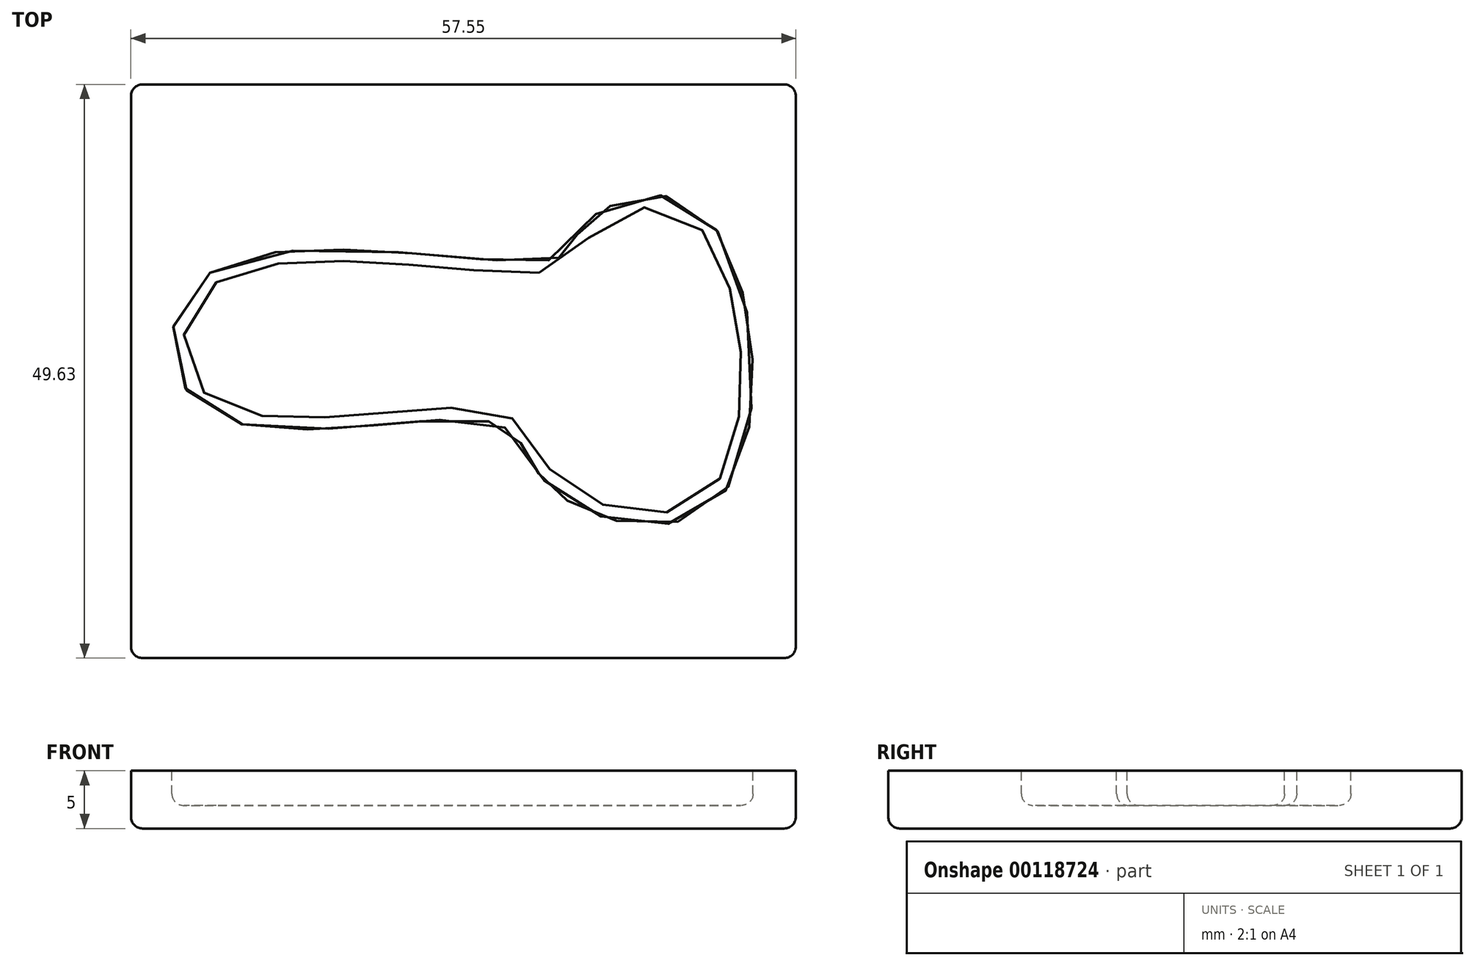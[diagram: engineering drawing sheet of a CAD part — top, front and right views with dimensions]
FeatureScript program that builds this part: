
annotation { "Feature Type Name" : "Feature", "Feature Type Description" : "" }
export const myFeature = defineFeature(function(context is Context, id is Id, definition is map)
    precondition{}
    {
        {
            var Q0;
            Q0=qCreatedBy(makeId("Top.planeOp"),FACE);
            var sketch = newSketch(context, id + "F0", { "sketchPlane" : qUnion([Q0])});
            skLineSegment(sketch, "E0.bottom", {"start": v(-57.55, 0) * mm, "end": v(0, 0) * mm});
            skLineSegment(sketch, "E0.top", {"start": v(-57.55, 49.63) * mm, "end": v(0, 49.63) * mm});
            skLineSegment(sketch, "E0.left", {"start": v(-57.55, 0) * mm, "end": v(-57.55, 49.63) * mm});
            skLineSegment(sketch, "E0.right", {"start": v(0, 0) * mm, "end": v(0, 49.63) * mm});
            skSolve(sketch);
        }
        {
            var Q0;
            Q0=makeQuery(id+"F0.imprint","IMPRINT",FACE,{"disambiguationData":[TD([[makeQuery(id+"F0.imprint","IMPRINT",EDGE,{"derivedFrom":sQuery(id+"F0.wireOp",EDGE,"E0.bottom")}),1.0]])]});
            extrude(context, id + "F1", {"entities" : qUnion([Q0]), "depth" : 5 * mm});
        }
        {
            var Q0;
            Q0=makeQuery(id+"F1.opExtrude","CAP_FACE",FACE,{"disambiguationData":[OSD([sQuery(id+"F0.wireOp",EDGE,"E0.bottom"),sQuery(id+"F0.wireOp",EDGE,"E0.top"),sQuery(id+"F0.wireOp",EDGE,"E0.left"),sQuery(id+"F0.wireOp",EDGE,"E0.right")])],"isStart":false});
            var sketch = newSketch(context, id + "F2", { "sketchPlane" : qUnion([Q0])});
            skFitSpline(sketch, "E1", {"points": [v(-50.7, 33.35) * mm, v(-20.78, 34.55) * mm, v(-18.4, 37.42) * mm, v(-8.54, 38.87) * mm, v(-6.24, 14.26) * mm, v(-18.4, 12.87) * mm, v(-22.88, 16.97) * mm, v(-26.54, 20.46) * mm, v(-50.99, 21.47) * mm, v(-50.7, 33.35) * mm]});
            skSolve(sketch);
        }
        {
            var Q0;
            Q0=makeQuery(id+"F2.imprint","IMPRINT",FACE,{"disambiguationData":[TD([[makeQuery(id+"F2.imprint","IMPRINT",EDGE,{"derivedFrom":sQuery(id+"F2.wireOp",EDGE,"E1")}),-1.0]])]});
            extrude(context, id + "F3", {"entities" : qUnion([Q0]), "operationType" : NewBodyOperationType.REMOVE, "oppositeDirection" : true, "depth" : 3 * mm});
        }
        {
            var Q0;
            Q0=makeQuery(id+"F3.boolean.opBoolean","COPY",FACE,{"derivedFrom":makeQuery(id+"F3.opExtrude","CAP_FACE",FACE,{"disambiguationData":[OSD([sQuery(id+"F2.wireOp",EDGE,"E1")])],"isStart":false})});
            fillet(context, id + "F4", {"entities" : qUnion([Q0]), "radius" : 1 * mm, "tangentPropagation" : true, "allowEdgeOverflow" : false});
        }
        {
            var Q0;
            Q0=makeQuery(id+"F1.opExtrude","CAP_FACE",FACE,{"disambiguationData":[OSD([sQuery(id+"F0.wireOp",EDGE,"E0.bottom"),sQuery(id+"F0.wireOp",EDGE,"E0.top"),sQuery(id+"F0.wireOp",EDGE,"E0.left"),sQuery(id+"F0.wireOp",EDGE,"E0.right")])],"isStart":true});
            fillet(context, id + "F5", {"entities" : qUnion([Q0]), "radius" : 1 * mm, "tangentPropagation" : true, "allowEdgeOverflow" : false});
        }
        {
            var Q0;
            Q0=makeQuery(id+"F1.opExtrude","SWEPT_EDGE",EDGE,{"disambiguationData":[OSD([sQuery(id+"F0.wireOp",EDGE,"E0.top"),sQuery(id+"F0.wireOp",EDGE,"E0.left")])]});
            var Q1;
            Q1=makeQuery(id+"F1.opExtrude","SWEPT_EDGE",EDGE,{"disambiguationData":[OSD([sQuery(id+"F0.wireOp",EDGE,"E0.bottom"),sQuery(id+"F0.wireOp",EDGE,"E0.right")])]});
            var Q2;
            Q2=makeQuery(id+"F1.opExtrude","SWEPT_EDGE",EDGE,{"disambiguationData":[OSD([sQuery(id+"F0.wireOp",EDGE,"E0.top"),sQuery(id+"F0.wireOp",EDGE,"E0.right")])]});
            var Q3;
            Q3=makeQuery(id+"F1.opExtrude","SWEPT_EDGE",EDGE,{"disambiguationData":[OSD([sQuery(id+"F0.wireOp",EDGE,"E0.bottom"),sQuery(id+"F0.wireOp",EDGE,"E0.left")])]});
            fillet(context, id + "F6", {"entities" : qUnion([Q0, Q1, Q2, Q3]), "radius" : 1 * mm, "tangentPropagation" : true, "allowEdgeOverflow" : false});
        }
    });
